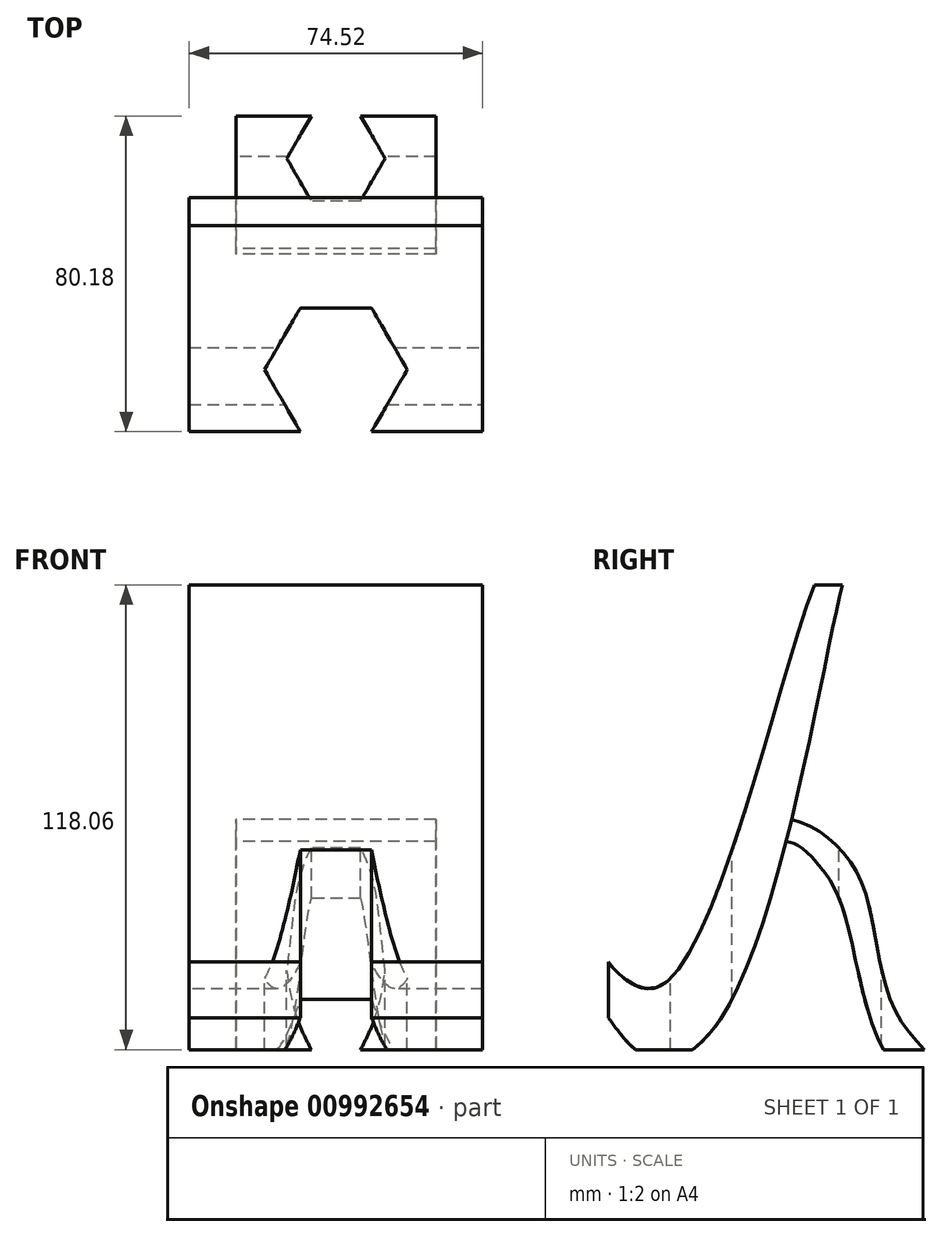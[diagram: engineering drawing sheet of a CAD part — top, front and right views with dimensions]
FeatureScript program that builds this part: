
annotation { "Feature Type Name" : "Feature", "Feature Type Description" : "" }
export const myFeature = defineFeature(function(context is Context, id is Id, definition is map)
    precondition{}
    {
        {
            var Q0;
            Q0=qCreatedBy(makeId("Front.planeOp"),FACE);
            var sketch = newSketch(context, id + "F0", { "sketchPlane" : qUnion([Q0])});
            skLineSegment(sketch, "E0.bottom", {"start": v(37.26, -59.69) * mm, "end": v(-37.26, -59.69) * mm});
            skLineSegment(sketch, "E0.top", {"start": v(37.26, 59.69) * mm, "end": v(-37.26, 59.69) * mm});
            skLineSegment(sketch, "E0.left", {"start": v(37.26, -59.69) * mm, "end": v(37.26, 59.69) * mm});
            skLineSegment(sketch, "E0.right", {"start": v(-37.26, -59.69) * mm, "end": v(-37.26, 59.69) * mm});
            skPoint(sketch, "E0.middle", {"position": v(0, 0) * mm});
            skSolve(sketch);
        }
        {
            var Q0;
            Q0 = qSketchRegion(id + "F0", true);
            extrude(context, id + "F1", {"entities" : qUnion([Q0]), "endBound" : BoundingType.SYMMETRIC, "depth" : 60 * mm, "offsetDistance" : 25 * mm});
        }
        {
            var Q0;
            Q0=makeQuery(id+"F1.opExtrude","SWEPT_FACE",FACE,{"disambiguationData":[OSD([sQuery(id+"F0.wireOp",EDGE,"E0.top")])]});
            var sketch = newSketch(context, id + "F2", { "sketchPlane" : qUnion([Q0])});
            skCircle(sketch, "E1.cCircle", {"center": v(0, -14.31) * mm, "radius": 15.69 * mm, "construction": true});
            skLineSegment(sketch, "E1.0", {"start": v(9.06, -30) * mm, "end": v(-9.06, -30) * mm});
            skLineSegment(sketch, "E1.1", {"start": v(-9.06, -30) * mm, "end": v(-18.11, -14.31) * mm});
            skLineSegment(sketch, "E1.2", {"start": v(-18.11, -14.31) * mm, "end": v(-9.06, 1.38) * mm});
            skLineSegment(sketch, "E1.3", {"start": v(-9.06, 1.38) * mm, "end": v(9.06, 1.38) * mm});
            skLineSegment(sketch, "E1.4", {"start": v(9.06, 1.38) * mm, "end": v(18.11, -14.31) * mm});
            skLineSegment(sketch, "E1.5", {"start": v(18.11, -14.31) * mm, "end": v(9.06, -30) * mm});
            skPoint(sketch, "E1.0.midPoint", {"position": v(0, -30) * mm});
            skSolve(sketch);
        }
        {
            var Q0;
            Q0 = qSketchRegion(id + "F2", true);
            extrude(context, id + "F3", {"entities" : qUnion([Q0]), "operationType" : NewBodyOperationType.REMOVE, "endBound" : BoundingType.THROUGH_ALL, "oppositeDirection" : true, "depth" : 25 * mm, "offsetDistance" : 25 * mm});
        }
        {
            var Q0;
            Q0=qCreatedBy(makeId("Right.planeOp"),FACE);
            var sketch = newSketch(context, id + "F4", { "sketchPlane" : qUnion([Q0])});
            skFitSpline(sketch, "E2", {"points": [v(-30.8, -34.36) * mm, v(-28.7, -37.8) * mm, v(-17.08, -42.28) * mm, v(22.23, 59.56) * mm, v(23.8, 76.7) * mm, v(-51.38, 66.15) * mm, v(-30.8, -34.36) * mm]});
            skSolve(sketch);
        }
        {
            var Q0;
            Q0 = qSketchRegion(id + "F4", true);
            extrude(context, id + "F5", {"entities" : qUnion([Q0]), "operationType" : NewBodyOperationType.REMOVE, "endBound" : BoundingType.SYMMETRIC, "oppositeDirection" : true, "depth" : 94 * mm, "offsetDistance" : 25 * mm});
        }
        {
            var Q0;
            Q0=qCreatedBy(makeId("Right.planeOp"),FACE);
            var sketch = newSketch(context, id + "F6", { "sketchPlane" : qUnion([Q0])});
            skFitSpline(sketch, "E3", {"points": [v(-31.06, -48.87) * mm, v(-20.25, -60.22) * mm, v(0, -48.08) * mm, v(29.35, 59.56) * mm, v(32.78, 67.2) * mm, v(41.49, 74.33) * mm, v(70.5, 69.05) * mm, v(93.99, -14.05) * mm, v(22.23, -72.35) * mm, v(-55.6, -52.3) * mm, v(-48.21, -46.5) * mm, v(-36.08, -45.18) * mm, v(-31.06, -48.87) * mm]});
            skSolve(sketch);
        }
        {
            var Q0;
            Q0 = qSketchRegion(id + "F6", true);
            extrude(context, id + "F7", {"entities" : qUnion([Q0]), "operationType" : NewBodyOperationType.REMOVE, "endBound" : BoundingType.SYMMETRIC, "oppositeDirection" : true, "depth" : 83.6 * mm, "offsetDistance" : 25 * mm});
        }
        {
            var Q0;
            Q0=qCreatedBy(makeId("Right.planeOp"),FACE);
            var sketch = newSketch(context, id + "F8", { "sketchPlane" : qUnion([Q0])});
            skFitSpline(sketch, "E4", {"points": [v(17.08, 0) * mm, v(33.97, -15.1) * mm, v(43.46, -49.66) * mm, v(53.75, -64.17) * mm, v(43.46, -62.85) * mm, v(30, -24.07) * mm, v(22.89, -10.88) * mm, v(17.6, -6.13) * mm, v(13.92, -5.08) * mm, v(8.64, 0) * mm, v(17.08, 0) * mm]});
            skSolve(sketch);
        }
        {
            var Q0;
            Q0 = qSketchRegion(id + "F8", true);
            extrude(context, id + "F9", {"entities" : qUnion([Q0]), "operationType" : NewBodyOperationType.ADD, "endBound" : BoundingType.SYMMETRIC, "depth" : 50.8 * mm, "offsetDistance" : 25 * mm});
        }
        {
            var Q0;
            Q0=qCreatedBy(makeId("Right.planeOp"),FACE);
            var sketch = newSketch(context, id + "F10", { "sketchPlane" : qUnion([Q0])});
            skLineSegment(sketch, "E5.bottom", {"start": v(66.68, -58.37) * mm, "end": v(-52.83, -58.37) * mm});
            skLineSegment(sketch, "E5.top", {"start": v(66.68, -74.46) * mm, "end": v(-52.83, -74.46) * mm});
            skLineSegment(sketch, "E5.left", {"start": v(66.68, -58.37) * mm, "end": v(66.68, -74.46) * mm});
            skLineSegment(sketch, "E5.right", {"start": v(-52.83, -58.37) * mm, "end": v(-52.83, -74.46) * mm});
            skSolve(sketch);
        }
        {
            var Q0;
            Q0 = qSketchRegion(id + "F10", true);
            extrude(context, id + "F11", {"entities" : qUnion([Q0]), "operationType" : NewBodyOperationType.REMOVE, "endBound" : BoundingType.SYMMETRIC, "oppositeDirection" : true, "depth" : 80.6 * mm, "offsetDistance" : 25 * mm});
        }
        {
            var Q0;
            Q0=qCreatedBy(makeId("Top.planeOp"),FACE);
            var sketch = newSketch(context, id + "F12", { "sketchPlane" : qUnion([Q0])});
            skCircle(sketch, "E6.cCircle", {"center": v(0, 39.37) * mm, "radius": 10.82 * mm, "construction": true});
            skLineSegment(sketch, "E6.0", {"start": v(-6.24, 50.2) * mm, "end": v(6.24, 50.2) * mm});
            skLineSegment(sketch, "E6.1", {"start": v(6.24, 50.2) * mm, "end": v(12.49, 39.37) * mm});
            skLineSegment(sketch, "E6.2", {"start": v(12.49, 39.37) * mm, "end": v(6.24, 28.56) * mm});
            skLineSegment(sketch, "E6.3", {"start": v(6.24, 28.56) * mm, "end": v(-6.24, 28.56) * mm});
            skLineSegment(sketch, "E6.4", {"start": v(-6.24, 28.56) * mm, "end": v(-12.49, 39.37) * mm});
            skLineSegment(sketch, "E6.5", {"start": v(-12.49, 39.37) * mm, "end": v(-6.24, 50.2) * mm});
            skPoint(sketch, "E6.0.midPoint", {"position": v(0, 50.2) * mm});
            skSolve(sketch);
        }
        {
            var Q0;
            Q0 = qSketchRegion(id + "F12", true);
            extrude(context, id + "F13", {"entities" : qUnion([Q0]), "operationType" : NewBodyOperationType.REMOVE, "oppositeDirection" : true, "depth" : 67 * mm, "offsetDistance" : 25 * mm});
        }
    });
